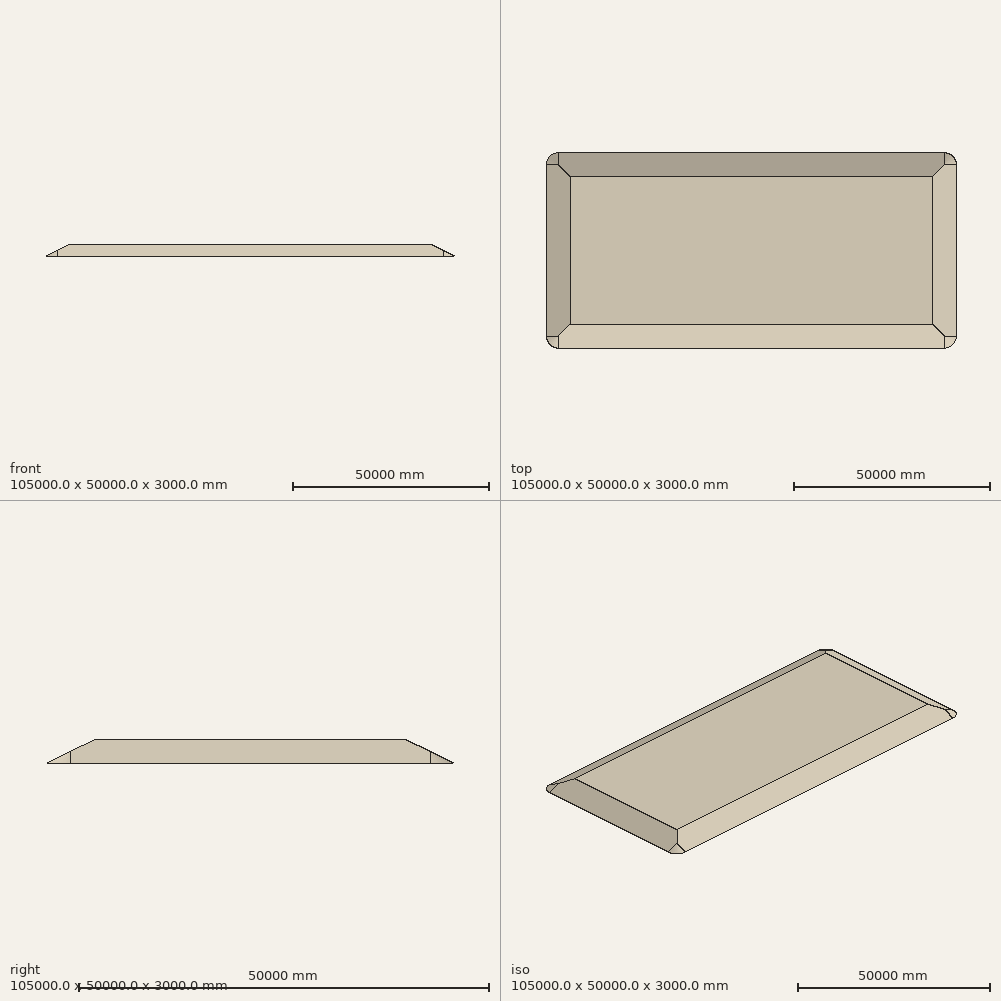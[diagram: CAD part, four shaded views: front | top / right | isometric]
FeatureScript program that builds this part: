
annotation { "Feature Type Name" : "Feature", "Feature Type Description" : "" }
export const myFeature = defineFeature(function(context is Context, id is Id, definition is map)
    precondition{}
    {
        {
            var Q0;
            Q0=qCreatedBy(makeId("Top.planeOp"),FACE);
            var sketch = newSketch(context, id + "F0", { "sketchPlane" : qUnion([Q0])});
            skLineSegment(sketch, "E0.bottom", {"start": v(-101873.3, 50980.58) * mm, "end": v(-3023.3, 50980.58) * mm});
            skLineSegment(sketch, "E0.top", {"start": v(-101873.3, 980.58) * mm, "end": v(-3023.3, 980.58) * mm});
            skLineSegment(sketch, "E0.left", {"start": v(-104948.3, 47905.58) * mm, "end": v(-104948.3, 4055.58) * mm});
            skLineSegment(sketch, "E0.right", {"start": v(51.7, 47905.58) * mm, "end": v(51.7, 4055.58) * mm});
            skPoint(sketch, "E1.visualSharp", {"position": v(-104948.3, 50980.58) * mm});
            skArc(sketch, "E1.filletArc", {"start": v(-101873.3, 50980.58) * mm, "mid": v(-104047.64, 50079.93) * mm, "end": v(-104948.3, 47905.58) * mm});
            skPoint(sketch, "E2.visualSharp", {"position": v(-104948.3, 980.58) * mm});
            skArc(sketch, "E2.filletArc", {"start": v(-104948.3, 4055.58) * mm, "mid": v(-104047.64, 1881.23) * mm, "end": v(-101873.3, 980.58) * mm});
            skPoint(sketch, "E3.visualSharp", {"position": v(51.7, 980.58) * mm});
            skArc(sketch, "E3.filletArc", {"start": v(-3023.3, 980.58) * mm, "mid": v(-848.94, 1881.23) * mm, "end": v(51.7, 4055.58) * mm});
            skPoint(sketch, "E4.visualSharp", {"position": v(51.7, 50980.58) * mm});
            skArc(sketch, "E4.filletArc", {"start": v(51.7, 47905.58) * mm, "mid": v(-848.94, 50079.93) * mm, "end": v(-3023.3, 50980.58) * mm});
            skSolve(sketch);
        }
        {
            var Q0;
            Q0=makeQuery(id+"F0.imprint","IMPRINT",FACE,{"disambiguationData":[TD([[makeQuery(id+"F0.imprint","IMPRINT",EDGE,{"derivedFrom":sQuery(id+"F0.wireOp",EDGE,"E0.bottom")}),-1.0]])]});
            extrude(context, id + "F1", {"entities" : qUnion([Q0]), "depth" : 3000 * mm, "hasDraft" : true, "draftAngle" : 64 * degree, "draftPullDirection" : true});
        }
    });
